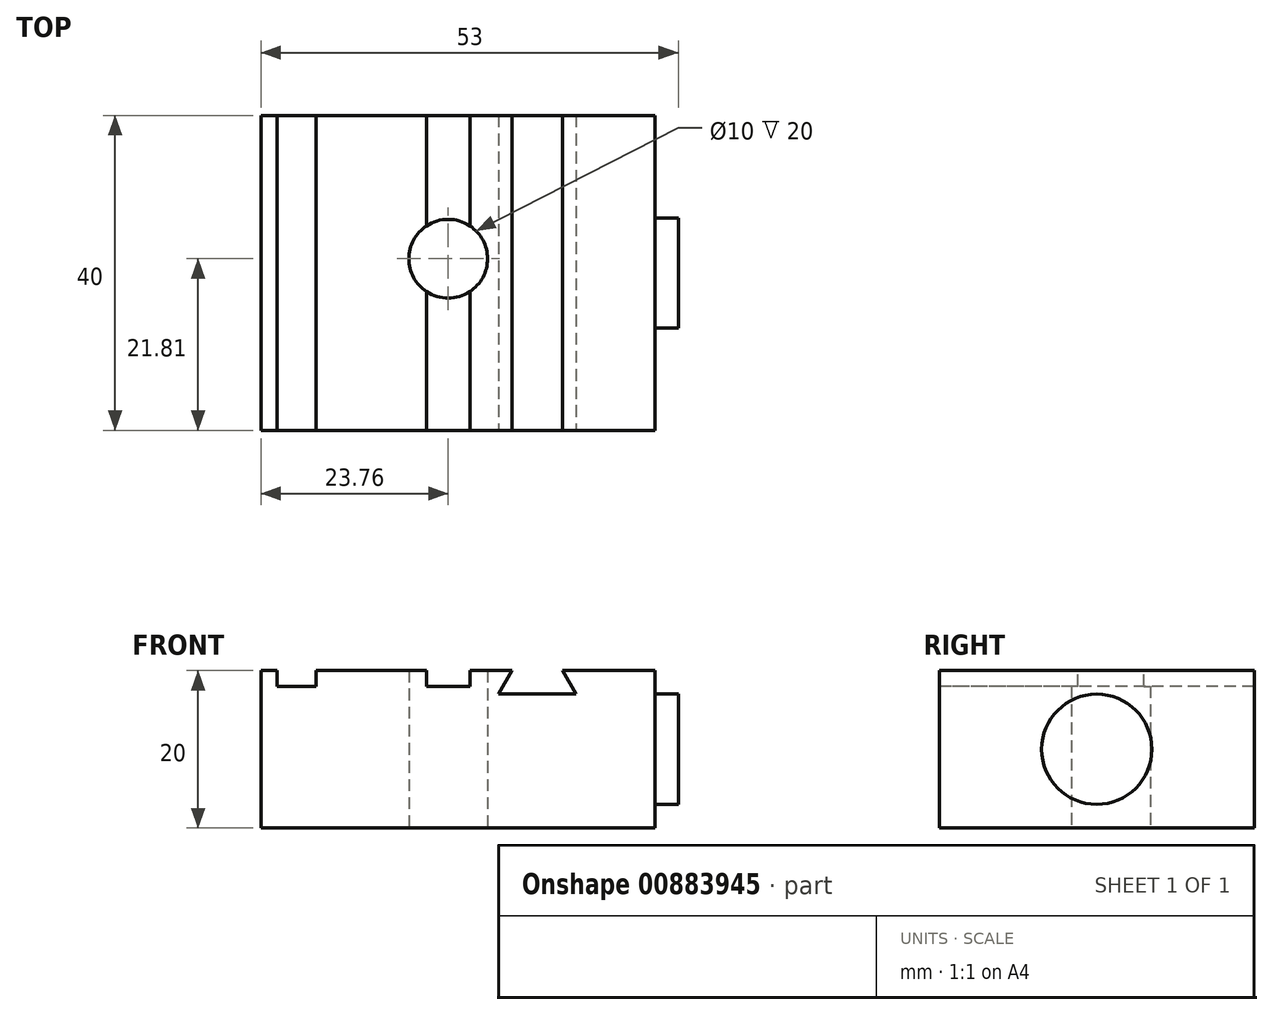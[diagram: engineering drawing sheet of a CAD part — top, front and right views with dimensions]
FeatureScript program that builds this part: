
annotation { "Feature Type Name" : "Feature", "Feature Type Description" : "" }
export const myFeature = defineFeature(function(context is Context, id is Id, definition is map)
    precondition{}
    {
        {
            var Q0;
            Q0=qCreatedBy(makeId("Top.planeOp"),FACE);
            var sketch = newSketch(context, id + "F0", { "sketchPlane" : qUnion([Q0])});
            skLineSegment(sketch, "E0.bottom", {"start": v(-23.76, 18.2) * mm, "end": v(26.24, 18.2) * mm});
            skLineSegment(sketch, "E0.top", {"start": v(-23.76, -21.8) * mm, "end": v(26.24, -21.8) * mm});
            skLineSegment(sketch, "E0.left", {"start": v(-23.76, 18.2) * mm, "end": v(-23.76, -21.8) * mm});
            skLineSegment(sketch, "E0.right", {"start": v(26.24, 18.2) * mm, "end": v(26.24, -21.8) * mm});
            skCircle(sketch, "E1", {"center": v(0, 0) * mm, "radius": 5 * mm});
            skSolve(sketch);
        }
        {
            var Q0;
            Q0=makeQuery(id+"F0.imprint","IMPRINT",FACE,{"disambiguationData":[TD([[makeQuery(id+"F0.imprint","IMPRINT",EDGE,{"derivedFrom":sQuery(id+"F0.wireOp",EDGE,"E0.bottom")}),-1.0]])]});
            extrude(context, id + "F1", {"entities" : qUnion([Q0]), "depth" : 20 * mm, "offsetDistance" : 25.4 * mm});
        }
        {
            var Q0;
            Q0=makeQuery(id+"F1.opExtrude","CAP_FACE",FACE,{"disambiguationData":[OSD([sQuery(id+"F0.wireOp",EDGE,"E0.bottom"),sQuery(id+"F0.wireOp",EDGE,"E0.top"),sQuery(id+"F0.wireOp",EDGE,"E0.left"),sQuery(id+"F0.wireOp",EDGE,"E0.right"),sQuery(id+"F0.wireOp",EDGE,"E1")])],"isStart":false});
            var sketch = newSketch(context, id + "F2", { "sketchPlane" : qUnion([Q0])});
            skLineSegment(sketch, "E2", {"start": v(-21.76, 18.2) * mm, "end": v(-21.76, -21.8) * mm});
            skLineSegment(sketch, "E3", {"start": v(-21.76, -21.8) * mm, "end": v(-16.76, -21.8) * mm});
            skLineSegment(sketch, "E4", {"start": v(-16.76, -21.8) * mm, "end": v(-16.76, 18.2) * mm});
            skLineSegment(sketch, "E5", {"start": v(-16.76, 18.2) * mm, "end": v(-21.76, 18.2) * mm});
            skLineSegment(sketch, "E6", {"start": v(-2.75, 18.2) * mm, "end": v(-2.75, -21.8) * mm});
            skLineSegment(sketch, "E7", {"start": v(-2.75, -21.8) * mm, "end": v(2.75, -21.8) * mm});
            skLineSegment(sketch, "E8", {"start": v(2.75, -21.8) * mm, "end": v(2.75, 18.2) * mm});
            skLineSegment(sketch, "E9", {"start": v(2.75, 18.2) * mm, "end": v(-2.75, 18.2) * mm});
            skPoint(sketch, "E10", {"position": v(0, 0) * mm});
            skLineSegment(sketch, "E11", {"start": v(0, 18.2) * mm, "end": v(0, -21.8) * mm, "construction": true});
            skSolve(sketch);
        }
        {
            var Q0;
            Q0=makeQuery(id+"F2.imprint","IMPRINT",FACE,{"disambiguationData":[TD([[makeQuery(id+"F2.imprint","IMPRINT",EDGE,{"derivedFrom":sQuery(id+"F2.wireOp",EDGE,"E2")}),1.0]])]});
            var Q1;
            {var subQ0=sQuery(id+"F2.wireOp",EDGE,"E7");Q1=makeQuery(id+"F2.imprint","IMPRINT",FACE,{"disambiguationData":[TD([[makeQuery(id+"F2.imprint","IMPRINT",EDGE,{"derivedFrom":subQ0}),1.0]])]});}
            var Q2;
            {var subQ0=sQuery(id+"F2.wireOp",EDGE,"E9");Q2=makeQuery(id+"F2.imprint","IMPRINT",FACE,{"disambiguationData":[TD([[makeQuery(id+"F2.imprint","IMPRINT",EDGE,{"derivedFrom":subQ0}),-1.0]])]});}
            extrude(context, id + "F3", {"entities" : qUnion([Q0, Q1, Q2]), "operationType" : NewBodyOperationType.REMOVE, "oppositeDirection" : true, "depth" : 2 * mm, "offsetDistance" : 25.4 * mm});
        }
        {
            var Q0;
            Q0=makeQuery(id+"F1.opExtrude","SWEPT_FACE",FACE,{"disambiguationData":[OSD([sQuery(id+"F0.wireOp",EDGE,"E0.top")])]});
            var sketch = newSketch(context, id + "F4", { "sketchPlane" : qUnion([Q0])});
            skLineSegment(sketch, "E12", {"start": v(8.1, 20) * mm, "end": v(6.38, 17) * mm});
            skLineSegment(sketch, "E13", {"start": v(6.38, 17) * mm, "end": v(16.23, 17) * mm});
            skLineSegment(sketch, "E14", {"start": v(16.23, 17) * mm, "end": v(14.5, 20) * mm});
            skLineSegment(sketch, "E15", {"start": v(14.5, 20) * mm, "end": v(8.1, 20) * mm});
            skLineSegment(sketch, "E16", {"start": v(11.3, 17) * mm, "end": v(11.3, 20) * mm, "construction": true});
            skPoint(sketch, "E17", {"position": v(0, 18) * mm});
            skSolve(sketch);
        }
        {
            var Q0;
            Q0=makeQuery(id+"F4.imprint","IMPRINT",FACE,{"disambiguationData":[TD([[makeQuery(id+"F4.imprint","IMPRINT",EDGE,{"derivedFrom":sQuery(id+"F4.wireOp",EDGE,"E12")}),1.0]])]});
            extrude(context, id + "F5", {"entities" : qUnion([Q0]), "operationType" : NewBodyOperationType.REMOVE, "endBound" : BoundingType.THROUGH_ALL, "oppositeDirection" : true, "depth" : 25.4 * mm, "offsetDistance" : 25.4 * mm});
        }
        {
            var Q0;
            Q0=makeQuery(id+"F1.opExtrude","SWEPT_FACE",FACE,{"disambiguationData":[OSD([sQuery(id+"F0.wireOp",EDGE,"E0.right")])]});
            var sketch = newSketch(context, id + "F6", { "sketchPlane" : qUnion([Q0])});
            skCircle(sketch, "E18", {"center": v(-1.8, 10) * mm, "radius": 7 * mm});
            skPoint(sketch, "E18.centerSnap0", {"position": v(-1.8, 20) * mm});
            skPoint(sketch, "E18.centerSnap1", {"position": v(-21.8, 10) * mm});
            skSolve(sketch);
        }
        {
            var Q0;
            Q0=makeQuery(id+"F6.imprint","IMPRINT",FACE,{"disambiguationData":[TD([[makeQuery(id+"F6.imprint","IMPRINT",EDGE,{"derivedFrom":sQuery(id+"F6.wireOp",EDGE,"E18")}),1.0]])]});
            extrude(context, id + "F7", {"entities" : qUnion([Q0]), "operationType" : NewBodyOperationType.ADD, "depth" : 3 * mm, "offsetDistance" : 25.4 * mm});
        }
    });
